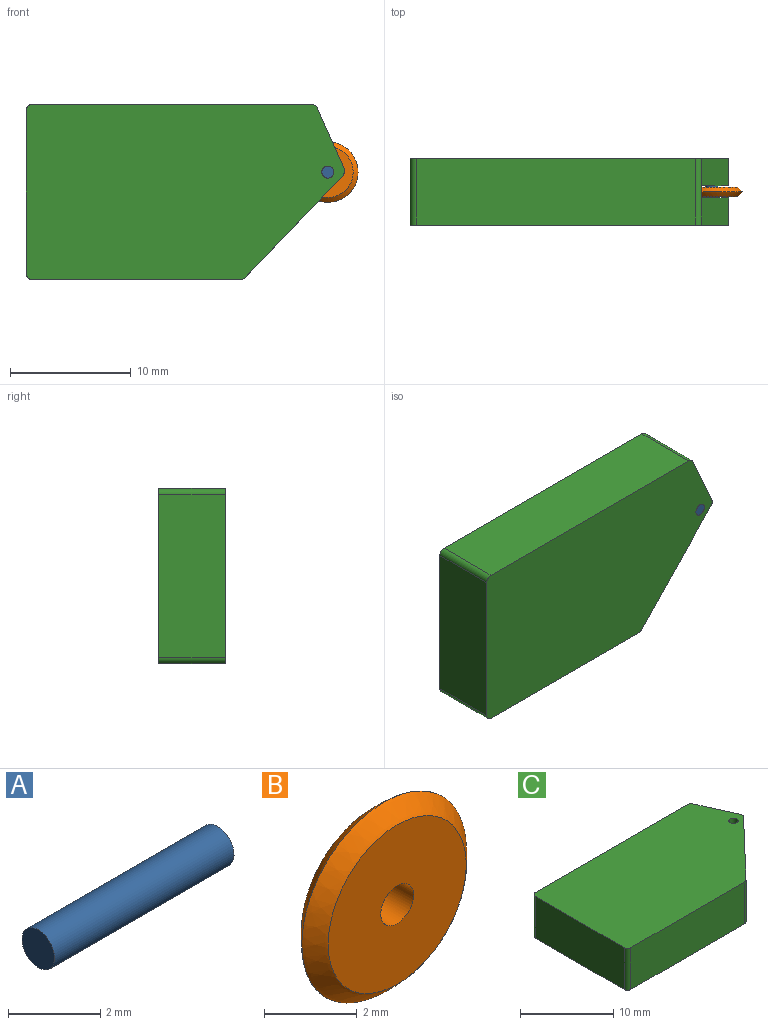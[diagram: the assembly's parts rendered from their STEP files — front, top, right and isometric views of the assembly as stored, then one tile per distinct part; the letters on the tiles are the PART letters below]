
ASSEMBLY  parts=3 mates=2
PART A: 3 faces, bbox 5.5x1x1 mm
  f0: plane 1x1mm, normal (-1,0,0), area 0.8mm2, adj f1
  f1: cylinder r=0.5mm len=5.5mm, axis (-1,0,0), area 17.3mm2, adj f0,f2
  f2: plane 1x1mm, normal (1,0,0), area 0.8mm2, adj f1
PART B: 5 faces, bbox 5x0.8x5 mm
  f0: plane 4.21x4.21mm, normal (0,-1,0), area 13.1mm2, adj f3,f4
  f1: plane 4.21x4.21mm, normal (0,1,0), area 13.1mm2, adj f2,f4
  f2: bspline ~5x4.99mm, area 8.2mm2, adj f1,f3
  f3: bspline ~5x4.99mm, area 8.2mm2, adj f0,f2
  f4: cylinder r=0.5mm len=1mm, axis (0,1,0), area 2.5mm2, adj f0,f1
PART C: 21 faces, bbox 26.4x14.5x5.5 mm
  f0: plane 5x2.25mm, normal (0.91,0.41,0), area 12.3mm2, adj f7,f12,f13,f17
  f1: plane 5x2.25mm, normal (0.91,0.41,0), area 12.3mm2, adj f6,f11,f16,f17
  f2: plane 8.5x8.12mm, normal (0.72,-0.69,0), area 53mm2, adj f6,f7,f9,f11,f12,f13,f15,f16
  f3: plane 13.5x5.5mm, normal (-1,0,0), area 74.2mm2, adj f6,f7,f14,f18
  f4: plane 17.29x5.5mm, normal (0,-1,0), area 95.1mm2, adj f6,f7,f14,f15
  f5: plane 23.18x5.5mm, normal (0,1,0), area 127.5mm2, adj f6,f7,f17,f18
  f6: plane 26.41x14.5mm, normal (0,0,1), area 338.5mm2, adj f1,f2,f3,f4,f5,f14,f15,f16
  f7: plane 26.41x14.5mm, normal (0,0,-1), area 338.5mm2, adj f0,f2,f3,f4,f5,f13,f14,f15
  f8: plane 14x1mm, normal (1,0,0), area 14mm2, adj f9,f10,f11,f12
  f9: plane 15.99x1mm, normal (0,1,0), area 16mm2, adj f2,f8,f11,f12
  f10: plane 21.86x1mm, normal (0,-1,0), area 21.9mm2, adj f8,f11,f12,f17
  f11: plane 24.16x14mm, normal (0,0,-1), area 296.6mm2, adj f1,f2,f8,f9,f10,f16,f17,f20
  f12: plane 24.16x14mm, normal (0,0,1), area 296.6mm2, adj f0,f2,f8,f9,f10,f13,f17,f19
  f13: cylinder r=0.5mm len=2.25mm, axis (0,0,-1), area 1.3mm2, adj f0,f2,f7,f12
  f14: cylinder r=0.5mm len=5.5mm, axis (0,0,1), area 4.3mm2, adj f3,f4,f6,f7
  f15: cylinder r=0.5mm len=5.5mm, axis (0,0,1), area 2.2mm2, adj f2,f4,f6,f7
  f16: cylinder r=0.5mm len=2.25mm, axis (0,0,-1), area 1.3mm2, adj f1,f2,f6,f11
  f17: cylinder r=0.5mm len=5.5mm, axis (0,0,-1), area 3.1mm2, adj f0,f1,f5,f6,f7,f10,f11,f12
  f18: cylinder r=0.5mm len=5.5mm, axis (0,0,-1), area 4.3mm2, adj f3,f5,f6,f7
  f19: cylinder r=0.5mm len=2.25mm, axis (0,0,-1), area 7.1mm2, adj f7,f12
  f20: cylinder r=0.5mm len=2.25mm, axis (0,0,-1), area 7.1mm2, adj f6,f11
PLACE A rot(axis=(0.58,-0.58,-0.58),120deg) t=(22.21,-5.45,7.25)mm
PLACE B t=(22.21,-7.8,7.25)mm
PLACE C rot(axis=(1,0,0),90deg) t=(-2.79,-5.45,-1.65)mm
MATE fastened B.f4 <-> A.f1  axis (0,1,0) through (22.21,-8.2,7.25)mm
MATE fastened A.f1 <-> C.f19  axis (0,1,0) through (22.21,-5.45,7.25)mm
